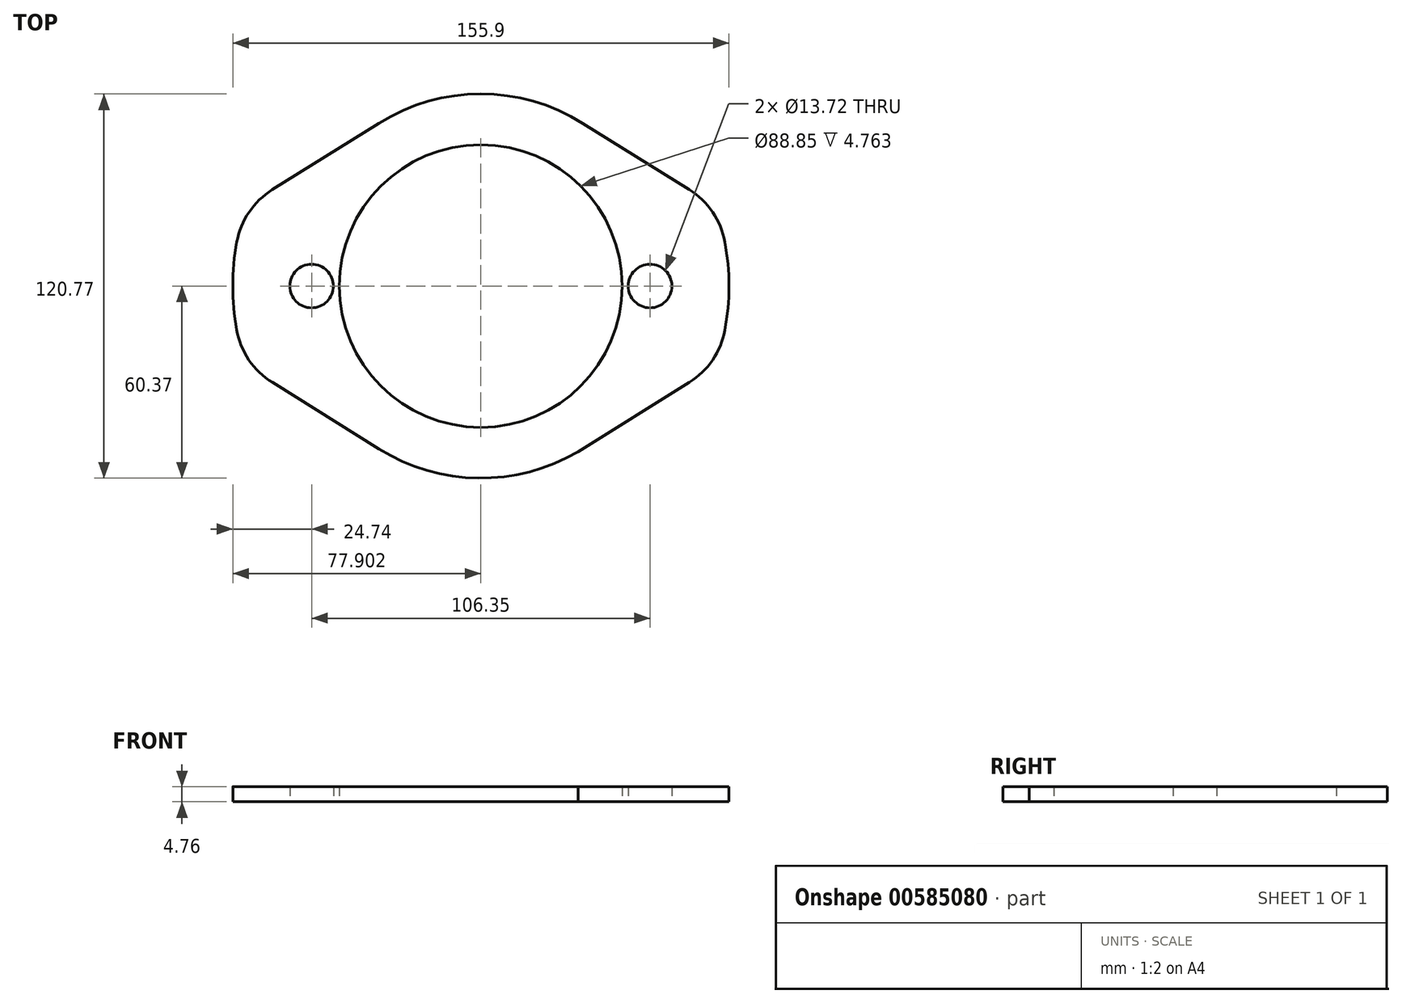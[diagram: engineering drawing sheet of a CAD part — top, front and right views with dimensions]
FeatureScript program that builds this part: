
annotation { "Feature Type Name" : "Feature", "Feature Type Description" : "" }
export const myFeature = defineFeature(function(context is Context, id is Id, definition is map)
    precondition{}
    {
        {
            var Q0;
            Q0=qCreatedBy(makeId("Top.planeOp"),FACE);
            var sketch = newSketch(context, id + "F0", { "sketchPlane" : qUnion([Q0])});
            skCircle(sketch, "E0", {"center": v(-9.86, 0) * mm, "radius": 6.86 * mm});
            skCircle(sketch, "E1", {"center": v(96.49, 0) * mm, "radius": 6.86 * mm});
            skCircle(sketch, "E2", {"center": v(43.3, 0) * mm, "radius": 44.42 * mm});
            skLineSegment(sketch, "E3", {"start": v(-9.86, 0) * mm, "end": v(43.3, 0) * mm});
            skLineSegment(sketch, "E4", {"start": v(-9.86, 0) * mm, "end": v(96.49, 0) * mm});
            skPoint(sketch, "E5.startSnap0", {"position": v(-16.21, 0) * mm});
            skArc(sketch, "E6", {"start": v(107.5, -11.52) * mm, "mid": v(108.6, 0) * mm, "end": v(107.5, 11.52) * mm});
            skArc(sketch, "E7", {"start": v(-20.87, 11.52) * mm, "mid": v(-21.9, 0) * mm, "end": v(-20.87, -11.52) * mm});
            skArc(sketch, "E8", {"start": v(-15.46, 19.52) * mm, "mid": v(-19, 16.08) * mm, "end": v(-20.87, 11.52) * mm});
            skArc(sketch, "E9", {"start": v(68.56, 40.46) * mm, "mid": v(43.3, 47.7) * mm, "end": v(18.04, 40.44) * mm});
            skArc(sketch, "E10", {"start": v(107.5, 11.52) * mm, "mid": v(105.65, 16.08) * mm, "end": v(102.1, 19.5) * mm});
            skArc(sketch, "E11", {"start": v(102.1, -19.5) * mm, "mid": v(105.65, -16.08) * mm, "end": v(107.5, -11.52) * mm});
            skArc(sketch, "E12", {"start": v(18.05, -40.44) * mm, "mid": v(42.58, -47.66) * mm, "end": v(67.33, -41.2) * mm});
            skArc(sketch, "E13", {"start": v(-20.87, -11.52) * mm, "mid": v(-19.03, -16.1) * mm, "end": v(-15.47, -19.5) * mm});
            skLineSegment(sketch, "E14", {"start": v(-15.47, -19.5) * mm, "end": v(18.05, -40.44) * mm});
            skLineSegment(sketch, "E15", {"start": v(67.33, -41.2) * mm, "end": v(102.1, -19.5) * mm});
            skLineSegment(sketch, "E16", {"start": v(18.04, 40.44) * mm, "end": v(-15.46, 19.52) * mm});
            skArc(sketch, "E17.0", {"start": v(-33.38, -13.72) * mm, "mid": v(-29.55, -23.22) * mm, "end": v(-22.16, -30.3) * mm});
            skArc(sketch, "E17.1", {"start": v(119.98, -13.86) * mm, "mid": v(121.3, 0) * mm, "end": v(119.99, 13.85) * mm});
            skArc(sketch, "E17.2", {"start": v(108.84, -30.26) * mm, "mid": v(116.14, -23.23) * mm, "end": v(119.98, -13.86) * mm});
            skLineSegment(sketch, "E17.3", {"start": v(73.9, -52.07) * mm, "end": v(108.84, -30.26) * mm});
            skArc(sketch, "E17.4", {"start": v(11.32, -51.21) * mm, "mid": v(42.5, -60.36) * mm, "end": v(73.9, -52.07) * mm});
            skArc(sketch, "E17.5", {"start": v(119.99, 13.85) * mm, "mid": v(116.14, 23.24) * mm, "end": v(108.83, 30.27) * mm});
            skLineSegment(sketch, "E17.6", {"start": v(-22.16, -30.3) * mm, "end": v(11.32, -51.21) * mm});
            skLineSegment(sketch, "E17.7", {"start": v(108.83, 30.27) * mm, "end": v(75.31, 51.21) * mm});
            skArc(sketch, "E17.8", {"start": v(75.31, 51.21) * mm, "mid": v(43.3, 60.4) * mm, "end": v(11.3, 51.2) * mm});
            skLineSegment(sketch, "E17.9", {"start": v(11.3, 51.2) * mm, "end": v(-22.22, 30.27) * mm});
            skArc(sketch, "E17.10", {"start": v(-22.22, 30.27) * mm, "mid": v(-29.51, 23.2) * mm, "end": v(-33.36, 13.81) * mm});
            skArc(sketch, "E17.11", {"start": v(-33.36, 13.81) * mm, "mid": v(-34.6, 0.05) * mm, "end": v(-33.38, -13.72) * mm});
            skSolve(sketch);
        }
        {
            var Q0;
            Q0=makeQuery(id+"F0.imprint","IMPRINT",FACE,{"disambiguationData":[TD([[makeQuery(id+"F0.imprint","IMPRINT",EDGE,{"derivedFrom":sQuery(id+"F0.wireOp",EDGE,"E0")}),-1.0]])]});
            extrude(context, id + "F1", {"entities" : qUnion([Q0]), "depth" : 4.76 * mm, "offsetDistance" : 25.4 * mm});
        }
    });
